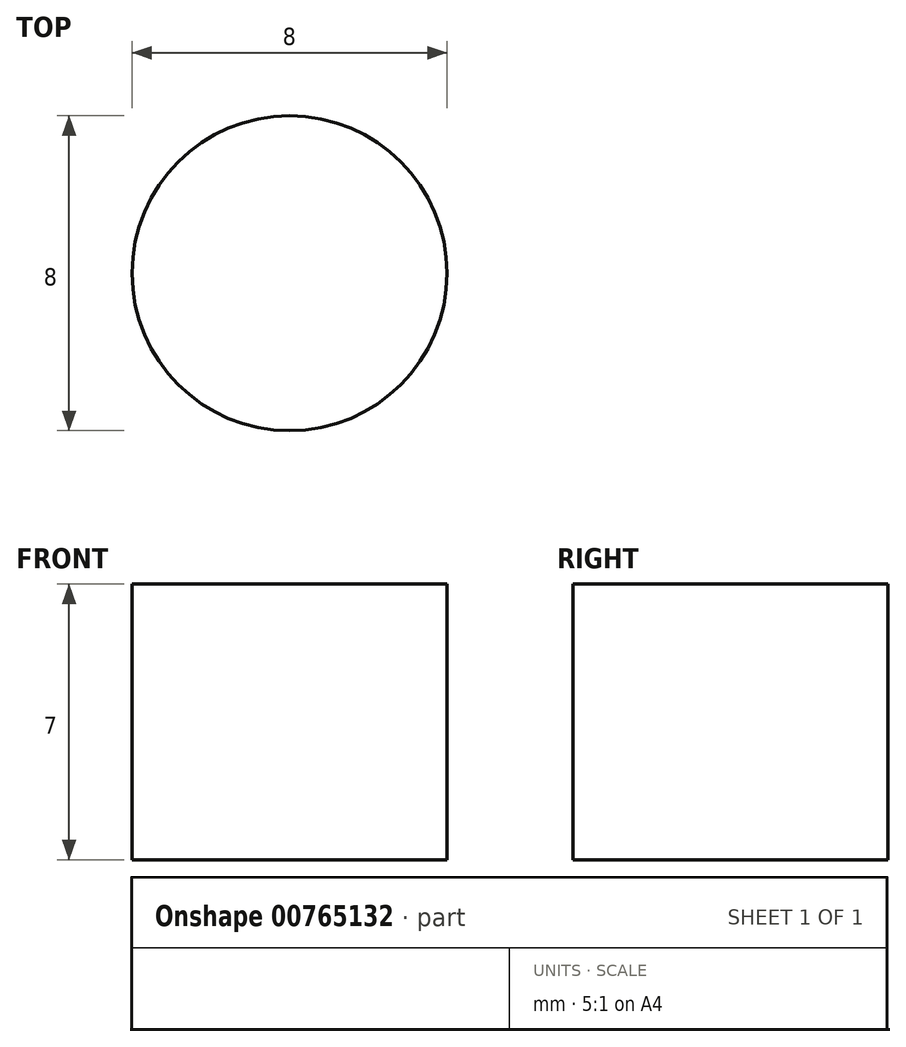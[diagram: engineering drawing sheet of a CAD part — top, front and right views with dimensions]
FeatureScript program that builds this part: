
annotation { "Feature Type Name" : "Feature", "Feature Type Description" : "" }
export const myFeature = defineFeature(function(context is Context, id is Id, definition is map)
    precondition{}
    {
        {
            var Q0;
            Q0=qCreatedBy(makeId("Top.planeOp"),FACE);
            var sketch = newSketch(context, id + "F0", { "sketchPlane" : qUnion([Q0])});
            skCircle(sketch, "E0", {"center": v(0, 0) * mm, "radius": 4 * mm});
            skSolve(sketch);
        }
        {
            var Q0;
            Q0=makeQuery(id+"F0.imprint","IMPRINT",FACE,{"disambiguationData":[TD([[makeQuery(id+"F0.imprint","IMPRINT",EDGE,{"derivedFrom":sQuery(id+"F0.wireOp",EDGE,"E0")}),1.0]])]});
            extrude(context, id + "F1", {"entities" : qUnion([Q0]), "depth" : 7 * mm, "offsetDistance" : 25 * mm});
        }
    });
